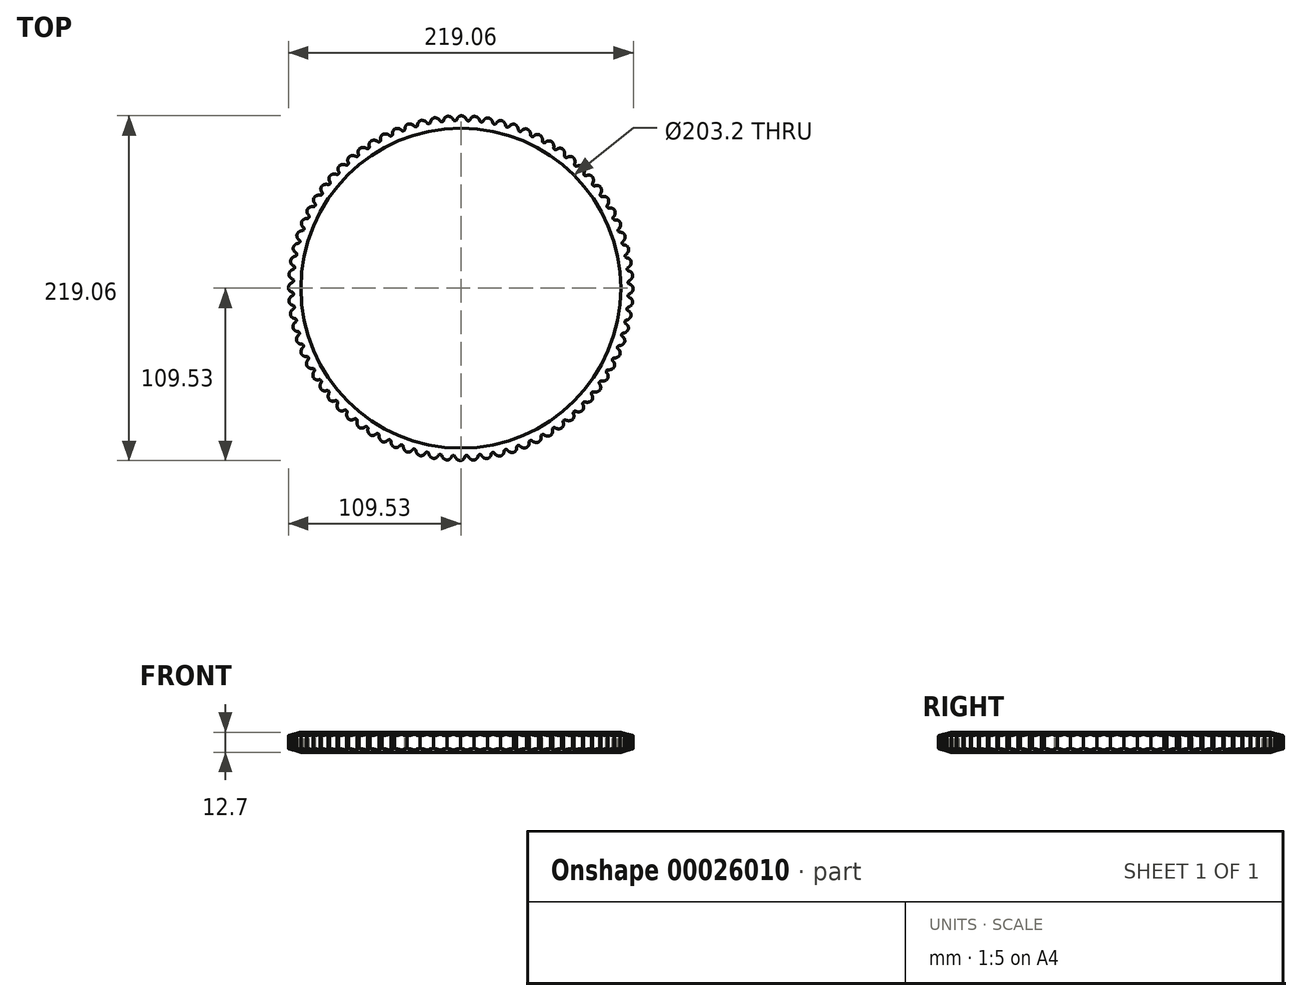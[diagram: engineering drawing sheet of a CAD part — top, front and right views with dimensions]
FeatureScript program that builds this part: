
annotation { "Feature Type Name" : "Feature", "Feature Type Description" : "" }
export const myFeature = defineFeature(function(context is Context, id is Id, definition is map)
    precondition{}
    {
        {
            var Q0;
            Q0=qCreatedBy(makeId("Top.planeOp"),FACE);
            var sketch = newSketch(context, id + "F0", { "sketchPlane" : qUnion([Q0])});
            skCircle(sketch, "E0", {"center": v(0, 0) * mm, "radius": 101.6 * mm});
            skCircle(sketch, "E1", {"center": v(0, 0) * mm, "radius": 109.54 * mm});
            skSolve(sketch);
        }
        {
            var Q0;
            Q0=qSketchRegion(id+"F0",true);
            extrude(context, id + "F1", {"entities" : qUnion([Q0]), "depth" : 12.7 * mm});
        }
        {
            var Q0;
            Q0=makeQuery(id+"F1.opExtrude","CAP_FACE",FACE,{"disambiguationData":[OSD([sQuery(id+"F0.wireOp",EDGE,"E0"),sQuery(id+"F0.wireOp",EDGE,"E1")])],"isStart":false});
            var sketch = newSketch(context, id + "F2", { "sketchPlane" : qUnion([Q0])});
            skLineSegment(sketch, "E2", {"start": v(0, 0) * mm, "end": v(0, 109.54) * mm, "construction": true});
            skArc(sketch, "E3", {"start": v(3.64, 107.03) * mm, "mid": v(2.2, 108.85) * mm, "end": v(0, 109.54) * mm});
            skCircle(sketch, "E4", {"center": v(0, 0) * mm, "radius": 106.36 * mm, "construction": true});
            skArc(sketch, "E5", {"start": v(9.16, 109.15) * mm, "mid": v(7.17, 108.66) * mm, "end": v(5.9, 107.06) * mm});
            skArc(sketch, "E6", {"start": v(3.64, 107.03) * mm, "mid": v(4.78, 106.26) * mm, "end": v(5.9, 107.06) * mm});
            skLineSegment(sketch, "E7", {"start": v(8.9, 106) * mm, "end": v(9.16, 109.15) * mm, "construction": true});
            skArc(sketch, "E8.1.0", {"start": v(-4.77, 106.99) * mm, "mid": v(-6.34, 108.69) * mm, "end": v(-8.6, 109.2) * mm});
            skArc(sketch, "E8.1.1", {"start": v(0.56, 109.54) * mm, "mid": v(-1.38, 108.89) * mm, "end": v(-2.52, 107.19) * mm});
            skArc(sketch, "E8.1.2", {"start": v(-4.77, 106.99) * mm, "mid": v(-3.57, 106.3) * mm, "end": v(-2.52, 107.19) * mm});
            skArc(sketch, "E8.2.0", {"start": v(-13.15, 106.28) * mm, "mid": v(-14.85, 107.86) * mm, "end": v(-17.14, 108.19) * mm});
            skArc(sketch, "E8.2.1", {"start": v(-8.03, 109.24) * mm, "mid": v(-9.92, 108.44) * mm, "end": v(-10.92, 106.66) * mm});
            skArc(sketch, "E8.2.2", {"start": v(-13.15, 106.28) * mm, "mid": v(-11.9, 105.7) * mm, "end": v(-10.92, 106.66) * mm});
            skArc(sketch, "E8.3.0", {"start": v(-21.45, 104.92) * mm, "mid": v(-23.26, 106.36) * mm, "end": v(-25.57, 106.51) * mm});
            skArc(sketch, "E8.3.1", {"start": v(-16.58, 108.28) * mm, "mid": v(-18.4, 107.33) * mm, "end": v(-19.26, 105.48) * mm});
            skArc(sketch, "E8.3.2", {"start": v(-21.45, 104.92) * mm, "mid": v(-20.16, 104.44) * mm, "end": v(-19.26, 105.48) * mm});
            skArc(sketch, "E8.4.0", {"start": v(-29.61, 102.92) * mm, "mid": v(-31.54, 104.2) * mm, "end": v(-33.85, 104.18) * mm});
            skArc(sketch, "E8.4.1", {"start": v(-25.02, 106.64) * mm, "mid": v(-26.76, 105.56) * mm, "end": v(-27.47, 103.64) * mm});
            skArc(sketch, "E8.4.2", {"start": v(-29.61, 102.92) * mm, "mid": v(-28.3, 102.53) * mm, "end": v(-27.47, 103.64) * mm});
            skArc(sketch, "E8.5.0", {"start": v(-37.6, 100.28) * mm, "mid": v(-39.61, 101.41) * mm, "end": v(-41.92, 101.2) * mm});
            skArc(sketch, "E8.5.1", {"start": v(-33.31, 104.35) * mm, "mid": v(-34.96, 103.13) * mm, "end": v(-35.52, 101.17) * mm});
            skArc(sketch, "E8.5.2", {"start": v(-37.6, 100.28) * mm, "mid": v(-36.25, 100) * mm, "end": v(-35.52, 101.17) * mm});
            skArc(sketch, "E8.6.0", {"start": v(-45.35, 97.02) * mm, "mid": v(-47.45, 97.99) * mm, "end": v(-49.73, 97.6) * mm});
            skArc(sketch, "E8.6.1", {"start": v(-41.4, 101.41) * mm, "mid": v(-42.94, 100.07) * mm, "end": v(-43.35, 98.07) * mm});
            skArc(sketch, "E8.6.2", {"start": v(-45.35, 97.02) * mm, "mid": v(-43.98, 96.85) * mm, "end": v(-43.35, 98.07) * mm});
            skArc(sketch, "E8.7.0", {"start": v(-52.82, 93.16) * mm, "mid": v(-55, 93.96) * mm, "end": v(-57.23, 93.4) * mm});
            skArc(sketch, "E8.7.1", {"start": v(-49.23, 97.85) * mm, "mid": v(-50.66, 96.4) * mm, "end": v(-50.9, 94.36) * mm});
            skArc(sketch, "E8.7.2", {"start": v(-52.82, 93.16) * mm, "mid": v(-51.44, 93.1) * mm, "end": v(-50.9, 94.36) * mm});
            skArc(sketch, "E8.8.0", {"start": v(-59.97, 88.73) * mm, "mid": v(-62.2, 89.36) * mm, "end": v(-64.38, 88.62) * mm});
            skArc(sketch, "E8.8.1", {"start": v(-56.75, 93.69) * mm, "mid": v(-58.07, 92.12) * mm, "end": v(-58.15, 90.08) * mm});
            skArc(sketch, "E8.8.2", {"start": v(-59.97, 88.73) * mm, "mid": v(-58.6, 88.77) * mm, "end": v(-58.15, 90.08) * mm});
            skArc(sketch, "E8.9.0", {"start": v(-66.74, 83.75) * mm, "mid": v(-69.01, 84.2) * mm, "end": v(-71.14, 83.3) * mm});
            skArc(sketch, "E8.9.1", {"start": v(-63.93, 88.95) * mm, "mid": v(-65.12, 87.28) * mm, "end": v(-65.04, 85.24) * mm});
            skArc(sketch, "E8.9.2", {"start": v(-66.74, 83.75) * mm, "mid": v(-65.37, 83.9) * mm, "end": v(-65.04, 85.24) * mm});
            skArc(sketch, "E8.10.0", {"start": v(-73.1, 78.26) * mm, "mid": v(-75.4, 78.53) * mm, "end": v(-77.45, 77.45) * mm});
            skArc(sketch, "E8.10.1", {"start": v(-70.7, 83.66) * mm, "mid": v(-71.76, 81.9) * mm, "end": v(-71.53, 79.87) * mm});
            skArc(sketch, "E8.10.2", {"start": v(-73.1, 78.26) * mm, "mid": v(-71.76, 78.51) * mm, "end": v(-71.53, 79.87) * mm});
            skArc(sketch, "E8.11.0", {"start": v(-79.02, 72.28) * mm, "mid": v(-81.34, 72.37) * mm, "end": v(-83.3, 71.14) * mm});
            skArc(sketch, "E8.11.1", {"start": v(-77.06, 77.85) * mm, "mid": v(-77.97, 76.02) * mm, "end": v(-77.58, 74.01) * mm});
            skArc(sketch, "E8.11.2", {"start": v(-79.02, 72.28) * mm, "mid": v(-77.7, 72.64) * mm, "end": v(-77.58, 74.01) * mm});
            skArc(sketch, "E8.12.0", {"start": v(-84.45, 65.86) * mm, "mid": v(-86.76, 65.77) * mm, "end": v(-88.62, 64.38) * mm});
            skArc(sketch, "E8.12.1", {"start": v(-82.93, 71.57) * mm, "mid": v(-83.7, 69.67) * mm, "end": v(-83.14, 67.7) * mm});
            skArc(sketch, "E8.12.2", {"start": v(-84.45, 65.86) * mm, "mid": v(-83.15, 66.32) * mm, "end": v(-83.14, 67.7) * mm});
            skArc(sketch, "E8.13.0", {"start": v(-89.36, 59.03) * mm, "mid": v(-91.66, 58.76) * mm, "end": v(-93.4, 57.23) * mm});
            skArc(sketch, "E8.13.1", {"start": v(-88.29, 64.84) * mm, "mid": v(-88.9, 62.89) * mm, "end": v(-88.2, 60.97) * mm});
            skArc(sketch, "E8.13.2", {"start": v(-89.36, 59.03) * mm, "mid": v(-88.1, 59.6) * mm, "end": v(-88.2, 60.97) * mm});
            skArc(sketch, "E8.14.0", {"start": v(-93.71, 51.83) * mm, "mid": v(-95.98, 51.39) * mm, "end": v(-97.6, 49.73) * mm});
            skArc(sketch, "E8.14.1", {"start": v(-93.1, 57.71) * mm, "mid": v(-93.56, 55.72) * mm, "end": v(-92.7, 53.86) * mm});
            skArc(sketch, "E8.14.2", {"start": v(-93.71, 51.83) * mm, "mid": v(-92.5, 52.5) * mm, "end": v(-92.7, 53.86) * mm});
            skArc(sketch, "E8.15.0", {"start": v(-97.5, 44.32) * mm, "mid": v(-99.72, 43.7) * mm, "end": v(-101.2, 41.92) * mm});
            skArc(sketch, "E8.15.1", {"start": v(-97.34, 50.23) * mm, "mid": v(-97.64, 48.2) * mm, "end": v(-96.65, 46.42) * mm});
            skArc(sketch, "E8.15.2", {"start": v(-97.5, 44.32) * mm, "mid": v(-96.34, 45.08) * mm, "end": v(-96.65, 46.42) * mm});
            skArc(sketch, "E8.16.0", {"start": v(-100.67, 36.54) * mm, "mid": v(-102.84, 35.74) * mm, "end": v(-104.18, 33.85) * mm});
            skArc(sketch, "E8.16.1", {"start": v(-100.98, 42.44) * mm, "mid": v(-101.13, 40.4) * mm, "end": v(-100, 38.7) * mm});
            skArc(sketch, "E8.16.2", {"start": v(-100.67, 36.54) * mm, "mid": v(-99.58, 37.38) * mm, "end": v(-100, 38.7) * mm});
            skArc(sketch, "E8.17.0", {"start": v(-103.22, 28.53) * mm, "mid": v(-105.33, 27.56) * mm, "end": v(-106.51, 25.57) * mm});
            skArc(sketch, "E8.17.1", {"start": v(-104, 34.38) * mm, "mid": v(-103.98, 32.34) * mm, "end": v(-102.72, 30.73) * mm});
            skArc(sketch, "E8.17.2", {"start": v(-103.22, 28.53) * mm, "mid": v(-102.2, 29.45) * mm, "end": v(-102.72, 30.73) * mm});
            skArc(sketch, "E8.18.0", {"start": v(-105.14, 20.34) * mm, "mid": v(-107.16, 19.21) * mm, "end": v(-108.19, 17.14) * mm});
            skArc(sketch, "E8.18.1", {"start": v(-106.38, 26.12) * mm, "mid": v(-106.2, 24.08) * mm, "end": v(-104.82, 22.57) * mm});
            skArc(sketch, "E8.18.2", {"start": v(-105.14, 20.34) * mm, "mid": v(-104.2, 21.34) * mm, "end": v(-104.82, 22.57) * mm});
            skArc(sketch, "E8.19.0", {"start": v(-106.42, 12.03) * mm, "mid": v(-108.34, 10.74) * mm, "end": v(-109.2, 8.6) * mm});
            skArc(sketch, "E8.19.1", {"start": v(-108.1, 17.7) * mm, "mid": v(-107.76, 15.67) * mm, "end": v(-106.26, 14.28) * mm});
            skArc(sketch, "E8.19.2", {"start": v(-106.42, 12.03) * mm, "mid": v(-105.55, 13.1) * mm, "end": v(-106.26, 14.28) * mm});
            skArc(sketch, "E8.20.0", {"start": v(-107.03, 3.64) * mm, "mid": v(-108.85, 2.2) * mm, "end": v(-109.54, 0) * mm});
            skArc(sketch, "E8.20.1", {"start": v(-109.15, 9.16) * mm, "mid": v(-108.66, 7.17) * mm, "end": v(-107.06, 5.9) * mm});
            skArc(sketch, "E8.20.2", {"start": v(-107.03, 3.64) * mm, "mid": v(-106.26, 4.78) * mm, "end": v(-107.06, 5.9) * mm});
            skArc(sketch, "E8.21.0", {"start": v(-106.99, -4.77) * mm, "mid": v(-108.69, -6.34) * mm, "end": v(-109.2, -8.6) * mm});
            skArc(sketch, "E8.21.1", {"start": v(-109.54, 0.56) * mm, "mid": v(-108.89, -1.38) * mm, "end": v(-107.19, -2.52) * mm});
            skArc(sketch, "E8.21.2", {"start": v(-106.99, -4.77) * mm, "mid": v(-106.3, -3.57) * mm, "end": v(-107.19, -2.52) * mm});
            skArc(sketch, "E8.22.0", {"start": v(-106.28, -13.15) * mm, "mid": v(-107.86, -14.85) * mm, "end": v(-108.19, -17.14) * mm});
            skArc(sketch, "E8.22.1", {"start": v(-109.24, -8.03) * mm, "mid": v(-108.44, -9.92) * mm, "end": v(-106.66, -10.92) * mm});
            skArc(sketch, "E8.22.2", {"start": v(-106.28, -13.15) * mm, "mid": v(-105.7, -11.9) * mm, "end": v(-106.66, -10.92) * mm});
            skArc(sketch, "E8.23.0", {"start": v(-104.92, -21.45) * mm, "mid": v(-106.36, -23.26) * mm, "end": v(-106.51, -25.57) * mm});
            skArc(sketch, "E8.23.1", {"start": v(-108.28, -16.58) * mm, "mid": v(-107.33, -18.4) * mm, "end": v(-105.48, -19.26) * mm});
            skArc(sketch, "E8.23.2", {"start": v(-104.92, -21.45) * mm, "mid": v(-104.44, -20.16) * mm, "end": v(-105.48, -19.26) * mm});
            skArc(sketch, "E8.24.0", {"start": v(-102.92, -29.61) * mm, "mid": v(-104.2, -31.54) * mm, "end": v(-104.18, -33.85) * mm});
            skArc(sketch, "E8.24.1", {"start": v(-106.64, -25.02) * mm, "mid": v(-105.56, -26.76) * mm, "end": v(-103.64, -27.47) * mm});
            skArc(sketch, "E8.24.2", {"start": v(-102.92, -29.61) * mm, "mid": v(-102.53, -28.3) * mm, "end": v(-103.64, -27.47) * mm});
            skArc(sketch, "E8.25.0", {"start": v(-100.28, -37.6) * mm, "mid": v(-101.41, -39.61) * mm, "end": v(-101.2, -41.92) * mm});
            skArc(sketch, "E8.25.1", {"start": v(-104.35, -33.31) * mm, "mid": v(-103.13, -34.96) * mm, "end": v(-101.17, -35.52) * mm});
            skArc(sketch, "E8.25.2", {"start": v(-100.28, -37.6) * mm, "mid": v(-100, -36.25) * mm, "end": v(-101.17, -35.52) * mm});
            skArc(sketch, "E8.26.0", {"start": v(-97.02, -45.35) * mm, "mid": v(-97.99, -47.45) * mm, "end": v(-97.6, -49.73) * mm});
            skArc(sketch, "E8.26.1", {"start": v(-101.41, -41.4) * mm, "mid": v(-100.07, -42.94) * mm, "end": v(-98.07, -43.35) * mm});
            skArc(sketch, "E8.26.2", {"start": v(-97.02, -45.35) * mm, "mid": v(-96.85, -43.98) * mm, "end": v(-98.07, -43.35) * mm});
            skArc(sketch, "E8.27.0", {"start": v(-93.16, -52.82) * mm, "mid": v(-93.96, -55) * mm, "end": v(-93.4, -57.23) * mm});
            skArc(sketch, "E8.27.1", {"start": v(-97.85, -49.23) * mm, "mid": v(-96.4, -50.66) * mm, "end": v(-94.36, -50.9) * mm});
            skArc(sketch, "E8.27.2", {"start": v(-93.16, -52.82) * mm, "mid": v(-93.1, -51.44) * mm, "end": v(-94.36, -50.9) * mm});
            skArc(sketch, "E8.28.0", {"start": v(-88.73, -59.97) * mm, "mid": v(-89.36, -62.2) * mm, "end": v(-88.62, -64.38) * mm});
            skArc(sketch, "E8.28.1", {"start": v(-93.69, -56.75) * mm, "mid": v(-92.12, -58.07) * mm, "end": v(-90.08, -58.15) * mm});
            skArc(sketch, "E8.28.2", {"start": v(-88.73, -59.97) * mm, "mid": v(-88.77, -58.6) * mm, "end": v(-90.08, -58.15) * mm});
            skArc(sketch, "E8.29.0", {"start": v(-83.75, -66.74) * mm, "mid": v(-84.2, -69.01) * mm, "end": v(-83.3, -71.14) * mm});
            skArc(sketch, "E8.29.1", {"start": v(-88.95, -63.93) * mm, "mid": v(-87.28, -65.12) * mm, "end": v(-85.24, -65.04) * mm});
            skArc(sketch, "E8.29.2", {"start": v(-83.75, -66.74) * mm, "mid": v(-83.9, -65.37) * mm, "end": v(-85.24, -65.04) * mm});
            skArc(sketch, "E8.30.0", {"start": v(-78.26, -73.1) * mm, "mid": v(-78.53, -75.4) * mm, "end": v(-77.45, -77.45) * mm});
            skArc(sketch, "E8.30.1", {"start": v(-83.66, -70.7) * mm, "mid": v(-81.9, -71.76) * mm, "end": v(-79.87, -71.53) * mm});
            skArc(sketch, "E8.30.2", {"start": v(-78.26, -73.1) * mm, "mid": v(-78.51, -71.76) * mm, "end": v(-79.87, -71.53) * mm});
            skArc(sketch, "E8.31.0", {"start": v(-72.28, -79.02) * mm, "mid": v(-72.37, -81.34) * mm, "end": v(-71.14, -83.3) * mm});
            skArc(sketch, "E8.31.1", {"start": v(-77.85, -77.06) * mm, "mid": v(-76.02, -77.97) * mm, "end": v(-74.01, -77.58) * mm});
            skArc(sketch, "E8.31.2", {"start": v(-72.28, -79.02) * mm, "mid": v(-72.64, -77.7) * mm, "end": v(-74.01, -77.58) * mm});
            skArc(sketch, "E8.32.0", {"start": v(-65.86, -84.45) * mm, "mid": v(-65.77, -86.76) * mm, "end": v(-64.38, -88.62) * mm});
            skArc(sketch, "E8.32.1", {"start": v(-71.57, -82.93) * mm, "mid": v(-69.67, -83.7) * mm, "end": v(-67.7, -83.14) * mm});
            skArc(sketch, "E8.32.2", {"start": v(-65.86, -84.45) * mm, "mid": v(-66.32, -83.15) * mm, "end": v(-67.7, -83.14) * mm});
            skArc(sketch, "E8.33.0", {"start": v(-59.03, -89.36) * mm, "mid": v(-58.76, -91.66) * mm, "end": v(-57.23, -93.4) * mm});
            skArc(sketch, "E8.33.1", {"start": v(-64.84, -88.29) * mm, "mid": v(-62.89, -88.9) * mm, "end": v(-60.97, -88.2) * mm});
            skArc(sketch, "E8.33.2", {"start": v(-59.03, -89.36) * mm, "mid": v(-59.6, -88.1) * mm, "end": v(-60.97, -88.2) * mm});
            skArc(sketch, "E8.34.0", {"start": v(-51.83, -93.71) * mm, "mid": v(-51.39, -95.98) * mm, "end": v(-49.73, -97.6) * mm});
            skArc(sketch, "E8.34.1", {"start": v(-57.71, -93.1) * mm, "mid": v(-55.72, -93.56) * mm, "end": v(-53.86, -92.7) * mm});
            skArc(sketch, "E8.34.2", {"start": v(-51.83, -93.71) * mm, "mid": v(-52.5, -92.5) * mm, "end": v(-53.86, -92.7) * mm});
            skArc(sketch, "E8.35.0", {"start": v(-44.32, -97.5) * mm, "mid": v(-43.7, -99.72) * mm, "end": v(-41.92, -101.2) * mm});
            skArc(sketch, "E8.35.1", {"start": v(-50.23, -97.34) * mm, "mid": v(-48.2, -97.64) * mm, "end": v(-46.42, -96.65) * mm});
            skArc(sketch, "E8.35.2", {"start": v(-44.32, -97.5) * mm, "mid": v(-45.08, -96.34) * mm, "end": v(-46.42, -96.65) * mm});
            skArc(sketch, "E8.36.0", {"start": v(-36.54, -100.67) * mm, "mid": v(-35.74, -102.84) * mm, "end": v(-33.85, -104.18) * mm});
            skArc(sketch, "E8.36.1", {"start": v(-42.44, -100.98) * mm, "mid": v(-40.4, -101.13) * mm, "end": v(-38.7, -100) * mm});
            skArc(sketch, "E8.36.2", {"start": v(-36.54, -100.67) * mm, "mid": v(-37.38, -99.58) * mm, "end": v(-38.7, -100) * mm});
            skArc(sketch, "E8.37.0", {"start": v(-28.53, -103.22) * mm, "mid": v(-27.56, -105.33) * mm, "end": v(-25.57, -106.51) * mm});
            skArc(sketch, "E8.37.1", {"start": v(-34.38, -104) * mm, "mid": v(-32.34, -103.98) * mm, "end": v(-30.73, -102.72) * mm});
            skArc(sketch, "E8.37.2", {"start": v(-28.53, -103.22) * mm, "mid": v(-29.45, -102.2) * mm, "end": v(-30.73, -102.72) * mm});
            skArc(sketch, "E8.38.0", {"start": v(-20.34, -105.14) * mm, "mid": v(-19.21, -107.16) * mm, "end": v(-17.14, -108.19) * mm});
            skArc(sketch, "E8.38.1", {"start": v(-26.12, -106.38) * mm, "mid": v(-24.08, -106.2) * mm, "end": v(-22.57, -104.82) * mm});
            skArc(sketch, "E8.38.2", {"start": v(-20.34, -105.14) * mm, "mid": v(-21.34, -104.2) * mm, "end": v(-22.57, -104.82) * mm});
            skArc(sketch, "E8.39.0", {"start": v(-12.03, -106.42) * mm, "mid": v(-10.74, -108.34) * mm, "end": v(-8.6, -109.2) * mm});
            skArc(sketch, "E8.39.1", {"start": v(-17.7, -108.1) * mm, "mid": v(-15.67, -107.76) * mm, "end": v(-14.28, -106.26) * mm});
            skArc(sketch, "E8.39.2", {"start": v(-12.03, -106.42) * mm, "mid": v(-13.1, -105.55) * mm, "end": v(-14.28, -106.26) * mm});
            skArc(sketch, "E8.40.0", {"start": v(-3.64, -107.03) * mm, "mid": v(-2.2, -108.85) * mm, "end": v(0, -109.54) * mm});
            skArc(sketch, "E8.40.1", {"start": v(-9.16, -109.15) * mm, "mid": v(-7.17, -108.66) * mm, "end": v(-5.9, -107.06) * mm});
            skArc(sketch, "E8.40.2", {"start": v(-3.64, -107.03) * mm, "mid": v(-4.78, -106.26) * mm, "end": v(-5.9, -107.06) * mm});
            skArc(sketch, "E8.41.0", {"start": v(4.77, -106.99) * mm, "mid": v(6.34, -108.69) * mm, "end": v(8.6, -109.2) * mm});
            skArc(sketch, "E8.41.1", {"start": v(-0.56, -109.54) * mm, "mid": v(1.38, -108.89) * mm, "end": v(2.52, -107.19) * mm});
            skArc(sketch, "E8.41.2", {"start": v(4.77, -106.99) * mm, "mid": v(3.57, -106.3) * mm, "end": v(2.52, -107.19) * mm});
            skArc(sketch, "E8.42.0", {"start": v(13.15, -106.28) * mm, "mid": v(14.85, -107.86) * mm, "end": v(17.14, -108.19) * mm});
            skArc(sketch, "E8.42.1", {"start": v(8.03, -109.24) * mm, "mid": v(9.92, -108.44) * mm, "end": v(10.92, -106.66) * mm});
            skArc(sketch, "E8.42.2", {"start": v(13.15, -106.28) * mm, "mid": v(11.9, -105.7) * mm, "end": v(10.92, -106.66) * mm});
            skArc(sketch, "E8.43.0", {"start": v(21.45, -104.92) * mm, "mid": v(23.26, -106.36) * mm, "end": v(25.57, -106.51) * mm});
            skArc(sketch, "E8.43.1", {"start": v(16.58, -108.28) * mm, "mid": v(18.4, -107.33) * mm, "end": v(19.26, -105.48) * mm});
            skArc(sketch, "E8.43.2", {"start": v(21.45, -104.92) * mm, "mid": v(20.16, -104.44) * mm, "end": v(19.26, -105.48) * mm});
            skArc(sketch, "E8.44.0", {"start": v(29.61, -102.92) * mm, "mid": v(31.54, -104.2) * mm, "end": v(33.85, -104.18) * mm});
            skArc(sketch, "E8.44.1", {"start": v(25.02, -106.64) * mm, "mid": v(26.76, -105.56) * mm, "end": v(27.47, -103.64) * mm});
            skArc(sketch, "E8.44.2", {"start": v(29.61, -102.92) * mm, "mid": v(28.3, -102.53) * mm, "end": v(27.47, -103.64) * mm});
            skArc(sketch, "E8.45.0", {"start": v(37.6, -100.28) * mm, "mid": v(39.61, -101.41) * mm, "end": v(41.92, -101.2) * mm});
            skArc(sketch, "E8.45.1", {"start": v(33.31, -104.35) * mm, "mid": v(34.96, -103.13) * mm, "end": v(35.52, -101.17) * mm});
            skArc(sketch, "E8.45.2", {"start": v(37.6, -100.28) * mm, "mid": v(36.25, -100) * mm, "end": v(35.52, -101.17) * mm});
            skArc(sketch, "E8.46.0", {"start": v(45.35, -97.02) * mm, "mid": v(47.45, -97.99) * mm, "end": v(49.73, -97.6) * mm});
            skArc(sketch, "E8.46.1", {"start": v(41.4, -101.41) * mm, "mid": v(42.94, -100.07) * mm, "end": v(43.35, -98.07) * mm});
            skArc(sketch, "E8.46.2", {"start": v(45.35, -97.02) * mm, "mid": v(43.98, -96.85) * mm, "end": v(43.35, -98.07) * mm});
            skArc(sketch, "E8.47.0", {"start": v(52.82, -93.16) * mm, "mid": v(55, -93.96) * mm, "end": v(57.23, -93.4) * mm});
            skArc(sketch, "E8.47.1", {"start": v(49.23, -97.85) * mm, "mid": v(50.66, -96.4) * mm, "end": v(50.9, -94.36) * mm});
            skArc(sketch, "E8.47.2", {"start": v(52.82, -93.16) * mm, "mid": v(51.44, -93.1) * mm, "end": v(50.9, -94.36) * mm});
            skArc(sketch, "E8.48.0", {"start": v(59.97, -88.73) * mm, "mid": v(62.2, -89.36) * mm, "end": v(64.38, -88.62) * mm});
            skArc(sketch, "E8.48.1", {"start": v(56.75, -93.69) * mm, "mid": v(58.07, -92.12) * mm, "end": v(58.15, -90.08) * mm});
            skArc(sketch, "E8.48.2", {"start": v(59.97, -88.73) * mm, "mid": v(58.6, -88.77) * mm, "end": v(58.15, -90.08) * mm});
            skArc(sketch, "E8.49.0", {"start": v(66.74, -83.75) * mm, "mid": v(69.01, -84.2) * mm, "end": v(71.14, -83.3) * mm});
            skArc(sketch, "E8.49.1", {"start": v(63.93, -88.95) * mm, "mid": v(65.12, -87.28) * mm, "end": v(65.04, -85.24) * mm});
            skArc(sketch, "E8.49.2", {"start": v(66.74, -83.75) * mm, "mid": v(65.37, -83.9) * mm, "end": v(65.04, -85.24) * mm});
            skArc(sketch, "E8.50.0", {"start": v(73.1, -78.26) * mm, "mid": v(75.4, -78.53) * mm, "end": v(77.45, -77.45) * mm});
            skArc(sketch, "E8.50.1", {"start": v(70.7, -83.66) * mm, "mid": v(71.76, -81.9) * mm, "end": v(71.53, -79.87) * mm});
            skArc(sketch, "E8.50.2", {"start": v(73.1, -78.26) * mm, "mid": v(71.76, -78.51) * mm, "end": v(71.53, -79.87) * mm});
            skArc(sketch, "E8.51.0", {"start": v(79.02, -72.28) * mm, "mid": v(81.34, -72.37) * mm, "end": v(83.3, -71.14) * mm});
            skArc(sketch, "E8.51.1", {"start": v(77.06, -77.85) * mm, "mid": v(77.97, -76.02) * mm, "end": v(77.58, -74.01) * mm});
            skArc(sketch, "E8.51.2", {"start": v(79.02, -72.28) * mm, "mid": v(77.7, -72.64) * mm, "end": v(77.58, -74.01) * mm});
            skArc(sketch, "E8.52.0", {"start": v(84.45, -65.86) * mm, "mid": v(86.76, -65.77) * mm, "end": v(88.62, -64.38) * mm});
            skArc(sketch, "E8.52.1", {"start": v(82.93, -71.57) * mm, "mid": v(83.7, -69.67) * mm, "end": v(83.14, -67.7) * mm});
            skArc(sketch, "E8.52.2", {"start": v(84.45, -65.86) * mm, "mid": v(83.15, -66.32) * mm, "end": v(83.14, -67.7) * mm});
            skArc(sketch, "E8.53.0", {"start": v(89.36, -59.03) * mm, "mid": v(91.66, -58.76) * mm, "end": v(93.4, -57.23) * mm});
            skArc(sketch, "E8.53.1", {"start": v(88.29, -64.84) * mm, "mid": v(88.9, -62.89) * mm, "end": v(88.2, -60.97) * mm});
            skArc(sketch, "E8.53.2", {"start": v(89.36, -59.03) * mm, "mid": v(88.1, -59.6) * mm, "end": v(88.2, -60.97) * mm});
            skArc(sketch, "E8.54.0", {"start": v(93.71, -51.83) * mm, "mid": v(95.98, -51.39) * mm, "end": v(97.6, -49.73) * mm});
            skArc(sketch, "E8.54.1", {"start": v(93.1, -57.71) * mm, "mid": v(93.56, -55.72) * mm, "end": v(92.7, -53.86) * mm});
            skArc(sketch, "E8.54.2", {"start": v(93.71, -51.83) * mm, "mid": v(92.5, -52.5) * mm, "end": v(92.7, -53.86) * mm});
            skArc(sketch, "E8.55.0", {"start": v(97.5, -44.32) * mm, "mid": v(99.72, -43.7) * mm, "end": v(101.2, -41.92) * mm});
            skArc(sketch, "E8.55.1", {"start": v(97.34, -50.23) * mm, "mid": v(97.64, -48.2) * mm, "end": v(96.65, -46.42) * mm});
            skArc(sketch, "E8.55.2", {"start": v(97.5, -44.32) * mm, "mid": v(96.34, -45.08) * mm, "end": v(96.65, -46.42) * mm});
            skArc(sketch, "E8.56.0", {"start": v(100.67, -36.54) * mm, "mid": v(102.84, -35.74) * mm, "end": v(104.18, -33.85) * mm});
            skArc(sketch, "E8.56.1", {"start": v(100.98, -42.44) * mm, "mid": v(101.13, -40.4) * mm, "end": v(100, -38.7) * mm});
            skArc(sketch, "E8.56.2", {"start": v(100.67, -36.54) * mm, "mid": v(99.58, -37.38) * mm, "end": v(100, -38.7) * mm});
            skArc(sketch, "E8.57.0", {"start": v(103.22, -28.53) * mm, "mid": v(105.33, -27.56) * mm, "end": v(106.51, -25.57) * mm});
            skArc(sketch, "E8.57.1", {"start": v(104, -34.38) * mm, "mid": v(103.98, -32.34) * mm, "end": v(102.72, -30.73) * mm});
            skArc(sketch, "E8.57.2", {"start": v(103.22, -28.53) * mm, "mid": v(102.2, -29.45) * mm, "end": v(102.72, -30.73) * mm});
            skArc(sketch, "E8.58.0", {"start": v(105.14, -20.34) * mm, "mid": v(107.16, -19.21) * mm, "end": v(108.19, -17.14) * mm});
            skArc(sketch, "E8.58.1", {"start": v(106.38, -26.12) * mm, "mid": v(106.2, -24.08) * mm, "end": v(104.82, -22.57) * mm});
            skArc(sketch, "E8.58.2", {"start": v(105.14, -20.34) * mm, "mid": v(104.2, -21.34) * mm, "end": v(104.82, -22.57) * mm});
            skArc(sketch, "E8.59.0", {"start": v(106.42, -12.03) * mm, "mid": v(108.34, -10.74) * mm, "end": v(109.2, -8.6) * mm});
            skArc(sketch, "E8.59.1", {"start": v(108.1, -17.7) * mm, "mid": v(107.76, -15.67) * mm, "end": v(106.26, -14.28) * mm});
            skArc(sketch, "E8.59.2", {"start": v(106.42, -12.03) * mm, "mid": v(105.55, -13.1) * mm, "end": v(106.26, -14.28) * mm});
            skArc(sketch, "E8.60.0", {"start": v(107.03, -3.64) * mm, "mid": v(108.85, -2.2) * mm, "end": v(109.54, 0) * mm});
            skArc(sketch, "E8.60.1", {"start": v(109.15, -9.16) * mm, "mid": v(108.66, -7.17) * mm, "end": v(107.06, -5.9) * mm});
            skArc(sketch, "E8.60.2", {"start": v(107.03, -3.64) * mm, "mid": v(106.26, -4.78) * mm, "end": v(107.06, -5.9) * mm});
            skArc(sketch, "E8.61.0", {"start": v(106.99, 4.77) * mm, "mid": v(108.69, 6.34) * mm, "end": v(109.2, 8.6) * mm});
            skArc(sketch, "E8.61.1", {"start": v(109.54, -0.56) * mm, "mid": v(108.89, 1.38) * mm, "end": v(107.19, 2.52) * mm});
            skArc(sketch, "E8.61.2", {"start": v(106.99, 4.77) * mm, "mid": v(106.3, 3.57) * mm, "end": v(107.19, 2.52) * mm});
            skArc(sketch, "E8.62.0", {"start": v(106.28, 13.15) * mm, "mid": v(107.86, 14.85) * mm, "end": v(108.19, 17.14) * mm});
            skArc(sketch, "E8.62.1", {"start": v(109.24, 8.03) * mm, "mid": v(108.44, 9.92) * mm, "end": v(106.66, 10.92) * mm});
            skArc(sketch, "E8.62.2", {"start": v(106.28, 13.15) * mm, "mid": v(105.7, 11.9) * mm, "end": v(106.66, 10.92) * mm});
            skArc(sketch, "E8.63.0", {"start": v(104.92, 21.45) * mm, "mid": v(106.36, 23.26) * mm, "end": v(106.51, 25.57) * mm});
            skArc(sketch, "E8.63.1", {"start": v(108.28, 16.58) * mm, "mid": v(107.33, 18.4) * mm, "end": v(105.48, 19.26) * mm});
            skArc(sketch, "E8.63.2", {"start": v(104.92, 21.45) * mm, "mid": v(104.44, 20.16) * mm, "end": v(105.48, 19.26) * mm});
            skArc(sketch, "E8.64.0", {"start": v(102.92, 29.61) * mm, "mid": v(104.2, 31.54) * mm, "end": v(104.18, 33.85) * mm});
            skArc(sketch, "E8.64.1", {"start": v(106.64, 25.02) * mm, "mid": v(105.56, 26.76) * mm, "end": v(103.64, 27.47) * mm});
            skArc(sketch, "E8.64.2", {"start": v(102.92, 29.61) * mm, "mid": v(102.53, 28.3) * mm, "end": v(103.64, 27.47) * mm});
            skArc(sketch, "E8.65.0", {"start": v(100.28, 37.6) * mm, "mid": v(101.41, 39.61) * mm, "end": v(101.2, 41.92) * mm});
            skArc(sketch, "E8.65.1", {"start": v(104.35, 33.31) * mm, "mid": v(103.13, 34.96) * mm, "end": v(101.17, 35.52) * mm});
            skArc(sketch, "E8.65.2", {"start": v(100.28, 37.6) * mm, "mid": v(100, 36.25) * mm, "end": v(101.17, 35.52) * mm});
            skArc(sketch, "E8.66.0", {"start": v(97.02, 45.35) * mm, "mid": v(97.99, 47.45) * mm, "end": v(97.6, 49.73) * mm});
            skArc(sketch, "E8.66.1", {"start": v(101.41, 41.4) * mm, "mid": v(100.07, 42.94) * mm, "end": v(98.07, 43.35) * mm});
            skArc(sketch, "E8.66.2", {"start": v(97.02, 45.35) * mm, "mid": v(96.85, 43.98) * mm, "end": v(98.07, 43.35) * mm});
            skArc(sketch, "E8.67.0", {"start": v(93.16, 52.82) * mm, "mid": v(93.96, 55) * mm, "end": v(93.4, 57.23) * mm});
            skArc(sketch, "E8.67.1", {"start": v(97.85, 49.23) * mm, "mid": v(96.4, 50.66) * mm, "end": v(94.36, 50.9) * mm});
            skArc(sketch, "E8.67.2", {"start": v(93.16, 52.82) * mm, "mid": v(93.1, 51.44) * mm, "end": v(94.36, 50.9) * mm});
            skArc(sketch, "E8.68.0", {"start": v(88.73, 59.97) * mm, "mid": v(89.36, 62.2) * mm, "end": v(88.62, 64.38) * mm});
            skArc(sketch, "E8.68.1", {"start": v(93.69, 56.75) * mm, "mid": v(92.12, 58.07) * mm, "end": v(90.08, 58.15) * mm});
            skArc(sketch, "E8.68.2", {"start": v(88.73, 59.97) * mm, "mid": v(88.77, 58.6) * mm, "end": v(90.08, 58.15) * mm});
            skArc(sketch, "E8.69.0", {"start": v(83.75, 66.74) * mm, "mid": v(84.2, 69.01) * mm, "end": v(83.3, 71.14) * mm});
            skArc(sketch, "E8.69.1", {"start": v(88.95, 63.93) * mm, "mid": v(87.28, 65.12) * mm, "end": v(85.24, 65.04) * mm});
            skArc(sketch, "E8.69.2", {"start": v(83.75, 66.74) * mm, "mid": v(83.9, 65.37) * mm, "end": v(85.24, 65.04) * mm});
            skArc(sketch, "E8.70.0", {"start": v(78.26, 73.1) * mm, "mid": v(78.53, 75.4) * mm, "end": v(77.45, 77.45) * mm});
            skArc(sketch, "E8.70.1", {"start": v(83.66, 70.7) * mm, "mid": v(81.9, 71.76) * mm, "end": v(79.87, 71.53) * mm});
            skArc(sketch, "E8.70.2", {"start": v(78.26, 73.1) * mm, "mid": v(78.51, 71.76) * mm, "end": v(79.87, 71.53) * mm});
            skArc(sketch, "E8.71.0", {"start": v(72.28, 79.02) * mm, "mid": v(72.37, 81.34) * mm, "end": v(71.14, 83.3) * mm});
            skArc(sketch, "E8.71.1", {"start": v(77.85, 77.06) * mm, "mid": v(76.02, 77.97) * mm, "end": v(74.01, 77.58) * mm});
            skArc(sketch, "E8.71.2", {"start": v(72.28, 79.02) * mm, "mid": v(72.64, 77.7) * mm, "end": v(74.01, 77.58) * mm});
            skArc(sketch, "E8.72.0", {"start": v(65.86, 84.45) * mm, "mid": v(65.77, 86.76) * mm, "end": v(64.38, 88.62) * mm});
            skArc(sketch, "E8.72.1", {"start": v(71.57, 82.93) * mm, "mid": v(69.67, 83.7) * mm, "end": v(67.7, 83.14) * mm});
            skArc(sketch, "E8.72.2", {"start": v(65.86, 84.45) * mm, "mid": v(66.32, 83.15) * mm, "end": v(67.7, 83.14) * mm});
            skArc(sketch, "E8.73.0", {"start": v(59.03, 89.36) * mm, "mid": v(58.76, 91.66) * mm, "end": v(57.23, 93.4) * mm});
            skArc(sketch, "E8.73.1", {"start": v(64.84, 88.29) * mm, "mid": v(62.89, 88.9) * mm, "end": v(60.97, 88.2) * mm});
            skArc(sketch, "E8.73.2", {"start": v(59.03, 89.36) * mm, "mid": v(59.6, 88.1) * mm, "end": v(60.97, 88.2) * mm});
            skArc(sketch, "E8.74.0", {"start": v(51.83, 93.71) * mm, "mid": v(51.39, 95.98) * mm, "end": v(49.73, 97.6) * mm});
            skArc(sketch, "E8.74.1", {"start": v(57.71, 93.1) * mm, "mid": v(55.72, 93.56) * mm, "end": v(53.86, 92.7) * mm});
            skArc(sketch, "E8.74.2", {"start": v(51.83, 93.71) * mm, "mid": v(52.5, 92.5) * mm, "end": v(53.86, 92.7) * mm});
            skArc(sketch, "E8.75.0", {"start": v(44.32, 97.5) * mm, "mid": v(43.7, 99.72) * mm, "end": v(41.92, 101.2) * mm});
            skArc(sketch, "E8.75.1", {"start": v(50.23, 97.34) * mm, "mid": v(48.2, 97.64) * mm, "end": v(46.42, 96.65) * mm});
            skArc(sketch, "E8.75.2", {"start": v(44.32, 97.5) * mm, "mid": v(45.08, 96.34) * mm, "end": v(46.42, 96.65) * mm});
            skArc(sketch, "E8.76.0", {"start": v(36.54, 100.67) * mm, "mid": v(35.74, 102.84) * mm, "end": v(33.85, 104.18) * mm});
            skArc(sketch, "E8.76.1", {"start": v(42.44, 100.98) * mm, "mid": v(40.4, 101.13) * mm, "end": v(38.7, 100) * mm});
            skArc(sketch, "E8.76.2", {"start": v(36.54, 100.67) * mm, "mid": v(37.38, 99.58) * mm, "end": v(38.7, 100) * mm});
            skArc(sketch, "E8.77.0", {"start": v(28.53, 103.22) * mm, "mid": v(27.56, 105.33) * mm, "end": v(25.57, 106.51) * mm});
            skArc(sketch, "E8.77.1", {"start": v(34.38, 104) * mm, "mid": v(32.34, 103.98) * mm, "end": v(30.73, 102.72) * mm});
            skArc(sketch, "E8.77.2", {"start": v(28.53, 103.22) * mm, "mid": v(29.45, 102.2) * mm, "end": v(30.73, 102.72) * mm});
            skArc(sketch, "E8.78.0", {"start": v(20.34, 105.14) * mm, "mid": v(19.21, 107.16) * mm, "end": v(17.14, 108.19) * mm});
            skArc(sketch, "E8.78.1", {"start": v(26.12, 106.38) * mm, "mid": v(24.08, 106.2) * mm, "end": v(22.57, 104.82) * mm});
            skArc(sketch, "E8.78.2", {"start": v(20.34, 105.14) * mm, "mid": v(21.34, 104.2) * mm, "end": v(22.57, 104.82) * mm});
            skArc(sketch, "E8.79.0", {"start": v(12.03, 106.42) * mm, "mid": v(10.74, 108.34) * mm, "end": v(8.6, 109.2) * mm});
            skArc(sketch, "E8.79.1", {"start": v(17.7, 108.1) * mm, "mid": v(15.67, 107.76) * mm, "end": v(14.28, 106.26) * mm});
            skArc(sketch, "E8.79.2", {"start": v(12.03, 106.42) * mm, "mid": v(13.1, 105.55) * mm, "end": v(14.28, 106.26) * mm});
            skCircle(sketch, "E9", {"center": v(0, 0) * mm, "radius": 129.3 * mm});
            skSolve(sketch);
        }
        {
            var Q0;
            Q0=qSketchRegion(id+"F2",true);
            extrude(context, id + "F3", {"entities" : qUnion([Q0]), "operationType" : NewBodyOperationType.REMOVE, "oppositeDirection" : true, "depth" : 25.4 * mm});
        }
        {
            var Q0;
            Q0=qCreatedBy(makeId("Top.planeOp"),FACE);
            var sketch = newSketch(context, id + "F4", { "sketchPlane" : qUnion([Q0])});
            skCircle(sketch, "E10", {"center": v(0, 0) * mm, "radius": 106.71 * mm});
            skSolve(sketch);
        }
        {
            var Q0;
            Q0=qSketchRegion(id+"F4",true);
            extrude(context, id + "F5", {"entities" : qUnion([Q0]), "depth" : 19.05 * mm, "hasSecondDirection" : true, "secondDirectionOppositeDirection" : true, "secondDirectionDepth" : 6.35 * mm});
        }
        {
            var Q0;
            Q0=makeQuery(id+"F5.opExtrude","CAP_EDGE",EDGE,{"disambiguationData":[OSD([sQuery(id+"F4.wireOp",EDGE,"E10")])],"isStart":false});
            var Q1;
            Q1=makeQuery(id+"F5.opExtrude","CAP_EDGE",EDGE,{"disambiguationData":[OSD([sQuery(id+"F4.wireOp",EDGE,"E10")])],"isStart":true});
            fillet(context, id + "F6", {"entities" : qUnion([Q0, Q1]), "radius" : 6.35 * mm, "tangentPropagation" : true, "allowEdgeOverflow" : false});
        }
        {
            var Q0;
            Q0=makeQuery(id+"F5.opExtrude","CAP_FACE",FACE,{"disambiguationData":[OSD([sQuery(id+"F4.wireOp",EDGE,"E10")])],"isStart":false});
            var sketch = newSketch(context, id + "F7", { "sketchPlane" : qUnion([Q0])});
            skArc(sketch, "E11", {"start": v(-85.48, 42.02) * mm, "mid": v(-95.25, 0) * mm, "end": v(-85.48, -42.02) * mm});
            skLineSegment(sketch, "E12.rect.left", {"start": v(6.35, 95.04) * mm, "end": v(6.35, 17.96) * mm});
            skLineSegment(sketch, "E12.rect.right", {"start": v(-6.35, 95.04) * mm, "end": v(-6.35, 17.96) * mm});
            skPoint(sketch, "E12.rect.top.end.orphan", {"position": v(-6.35, -100.16) * mm});
            skPoint(sketch, "E13.trimOffspring.end.orphan", {"position": v(6.35, -100.16) * mm});
            skPoint(sketch, "E14.orphan", {"position": v(6.35, 100.16) * mm});
            skPoint(sketch, "E15.orphan", {"position": v(-6.35, 100.16) * mm});
            skLineSegment(sketch, "E16.1.0", {"start": v(-85.48, 42.02) * mm, "end": v(-18.73, 3.48) * mm});
            skLineSegment(sketch, "E16.1.2", {"start": v(-79.13, 53.02) * mm, "end": v(-12.38, 14.48) * mm});
            skPoint(sketch, "E16.1.3", {"position": v(-89.92, 44.58) * mm});
            skPoint(sketch, "E16.1.4", {"position": v(-83.57, 55.58) * mm});
            skLineSegment(sketch, "E16.2.0", {"start": v(-79.13, -53.02) * mm, "end": v(-12.38, -14.48) * mm});
            skLineSegment(sketch, "E16.2.2", {"start": v(-85.48, -42.02) * mm, "end": v(-18.73, -3.48) * mm});
            skPoint(sketch, "E16.2.3", {"position": v(-83.57, -55.58) * mm});
            skPoint(sketch, "E16.2.4", {"position": v(-89.92, -44.58) * mm});
            skLineSegment(sketch, "E16.3.0", {"start": v(6.35, -95.04) * mm, "end": v(6.35, -17.96) * mm});
            skLineSegment(sketch, "E16.3.2", {"start": v(-6.35, -95.04) * mm, "end": v(-6.35, -17.96) * mm});
            skLineSegment(sketch, "E16.4.0", {"start": v(85.48, -42.02) * mm, "end": v(18.73, -3.48) * mm});
            skLineSegment(sketch, "E16.4.2", {"start": v(79.13, -53.02) * mm, "end": v(12.38, -14.48) * mm});
            skPoint(sketch, "E16.4.3", {"position": v(89.92, -44.58) * mm});
            skPoint(sketch, "E16.4.4", {"position": v(83.57, -55.58) * mm});
            skLineSegment(sketch, "E16.5.0", {"start": v(79.13, 53.02) * mm, "end": v(12.38, 14.48) * mm});
            skLineSegment(sketch, "E16.5.2", {"start": v(85.48, 42.02) * mm, "end": v(18.73, 3.48) * mm});
            skPoint(sketch, "E16.5.3", {"position": v(83.57, 55.58) * mm});
            skPoint(sketch, "E16.5.4", {"position": v(89.92, 44.58) * mm});
            skArc(sketch, "E17", {"start": v(-12.38, -14.48) * mm, "mid": v(-9.52, -16.5) * mm, "end": v(-6.35, -17.96) * mm});
            skArc(sketch, "E18.trimOffspring", {"start": v(-6.35, 95.04) * mm, "mid": v(-47.62, 82.49) * mm, "end": v(-79.13, 53.02) * mm});
            skArc(sketch, "E19.trimOffspring", {"start": v(79.13, 53.02) * mm, "mid": v(47.63, 82.49) * mm, "end": v(6.35, 95.04) * mm});
            skArc(sketch, "E20.trimOffspring", {"start": v(85.48, -42.02) * mm, "mid": v(95.25, 0) * mm, "end": v(85.48, 42.02) * mm});
            skArc(sketch, "E21.trimOffspring", {"start": v(6.35, -95.04) * mm, "mid": v(47.62, -82.49) * mm, "end": v(79.13, -53.02) * mm});
            skArc(sketch, "E22.trimOffspring", {"start": v(-79.13, -53.02) * mm, "mid": v(-47.63, -82.49) * mm, "end": v(-6.35, -95.04) * mm});
            skPoint(sketch, "E23.trimOffspring.end.orphan", {"position": v(-6.35, 0) * mm});
            skPoint(sketch, "E24.orphan", {"position": v(3.18, 5.5) * mm});
            skArc(sketch, "E25.trimOffspring", {"start": v(-18.73, 3.48) * mm, "mid": v(-19.05, 0) * mm, "end": v(-18.73, -3.48) * mm});
            skArc(sketch, "E26.trimOffspring", {"start": v(-6.35, 17.96) * mm, "mid": v(-9.52, 16.5) * mm, "end": v(-12.38, 14.48) * mm});
            skArc(sketch, "E27.trimOffspring", {"start": v(12.38, 14.48) * mm, "mid": v(9.53, 16.5) * mm, "end": v(6.35, 17.96) * mm});
            skPoint(sketch, "E28.orphan", {"position": v(6.35, 0) * mm});
            skArc(sketch, "E29.trimOffspring", {"start": v(6.35, -17.96) * mm, "mid": v(9.52, -16.5) * mm, "end": v(12.38, -14.48) * mm});
            skArc(sketch, "E30.trimOffspring", {"start": v(18.73, -3.48) * mm, "mid": v(19.05, 0) * mm, "end": v(18.73, 3.48) * mm});
            skSolve(sketch);
        }
        {
            var Q0;
            Q0=qSketchRegion(id+"F7",true);
            extrude(context, id + "F8", {"entities" : qUnion([Q0]), "operationType" : NewBodyOperationType.REMOVE, "endBound" : BoundingType.THROUGH_ALL, "oppositeDirection" : true, "depth" : 25.4 * mm});
        }
        {
            var Q0;
            Q0=makeQuery(id+"F5.opExtrude","CAP_FACE",FACE,{"disambiguationData":[OSD([sQuery(id+"F4.wireOp",EDGE,"E10")])],"isStart":false});
            var sketch = newSketch(context, id + "F9", { "sketchPlane" : qUnion([Q0])});
            skCircle(sketch, "E31", {"center": v(0, 0) * mm, "radius": 6.35 * mm});
            skSolve(sketch);
        }
        {
            var Q0;
            Q0=qSketchRegion(id+"F9",true);
            extrude(context, id + "F10", {"entities" : qUnion([Q0]), "operationType" : NewBodyOperationType.REMOVE, "endBound" : BoundingType.THROUGH_ALL, "oppositeDirection" : true, "depth" : 25.4 * mm});
        }
        {
            var Q0;
            Q0=makeQuery(id+"F5.opExtrude","SWEPT_BODY",BODY,{"disambiguationData":[OSD([sQuery(id+"F4.wireOp",EDGE,"E10")])]});
            deleteBodies(context, id + "F11", {"entities" : qUnion([Q0])});
        }
        {
            var Q0;
            Q0=qCreatedBy(makeId("Right.planeOp"),FACE);
            var sketch = newSketch(context, id + "F12", { "sketchPlane" : qUnion([Q0])});
            skLineSegment(sketch, "E32", {"start": v(-113.32, 3.36) * mm, "end": v(-113.32, 9.34) * mm});
            skLineSegment(sketch, "E33", {"start": v(-113.32, 9.34) * mm, "end": v(-101.6, 12.7) * mm});
            skLineSegment(sketch, "E34", {"start": v(-101.6, 0) * mm, "end": v(-113.32, 3.36) * mm});
            skLineSegment(sketch, "E35", {"start": v(-101.6, 0) * mm, "end": v(-101.6, 0) * mm});
            skLineSegment(sketch, "E36", {"start": v(-101.6, 0) * mm, "end": v(-119.18, 0) * mm});
            skLineSegment(sketch, "E37", {"start": v(-119.18, 0) * mm, "end": v(-119.18, 15.81) * mm});
            skLineSegment(sketch, "E38", {"start": v(-119.18, 15.81) * mm, "end": v(-101.6, 12.7) * mm});
            skLineSegment(sketch, "E39", {"start": v(0, 0) * mm, "end": v(0, -54.5) * mm, "construction": true});
            skSolve(sketch);
        }
        {
            var Q0;
            Q0=qSketchRegion(id+"F12",true);
            var Q1;
            Q1=sQuery(id+"F12.wireOp",EDGE,"E39");
            revolve(context, id + "F13", {"operationType" : NewBodyOperationType.REMOVE, "entities" : qUnion([Q0]), "axis" : qUnion([Q1]), "revolveType" : RevolveType.FULL, "oppositeDirection" : true});
        }
    });
